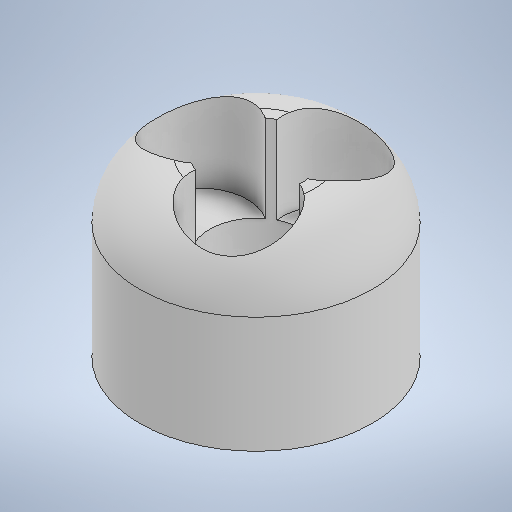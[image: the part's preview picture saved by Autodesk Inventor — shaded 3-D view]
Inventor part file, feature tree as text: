
AUTODESK INVENTOR PART (.ipt)
format: ipt  version: 2025.1 (Build 291241000, 241)  size: 266,240 bytes
history: native  units: in
note: dims shown in document units (in); Inventor stores cm internally (conversion verified against a paired STEP export)
features: extrude x2, sketch x1, fillet x1
ambient origin geometry x8: Origin, YZ Plane, XZ Plane, XY Plane, X Axis, Y Axis, Z Axis, Center Point
bodies: Solid1 (feature_tree)
feature tree (4):
  sketch  "Sketch1"  dims[d3=0.2in d7=0.2in d8=0.5in d9=0.1875in d10=0.0in d11=0.375in d12=0.0in d13=0.125in d14=0.2in d15=0.2in]
  extrude  "Extrusion1"  Depth=0.125in
  extrude  "Extrusion2"  Depth=0.125in
  fillet  "Fillet1"  Radius=0.1875in
